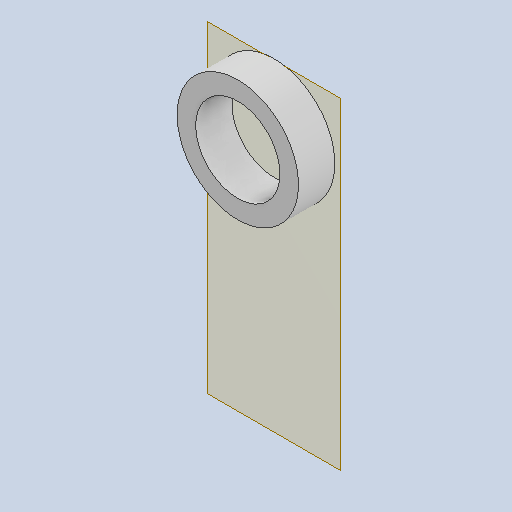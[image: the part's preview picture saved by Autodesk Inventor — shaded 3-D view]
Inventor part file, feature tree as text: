
AUTODESK INVENTOR PART (.ipt)
format: ipt  version: 2023 (Build 270158000, 158)  size: 333,824 bytes
history: native  units: mm
features: other x5, reference x2, plane x1, extrude x1, sketch x1
ambient origin geometry x8: Origin, YZ Plane, XZ Plane, XY Plane, X Axis, Y Axis, Z Axis, Center Point
bodies: Solid1 (feature_tree)
feature tree (10):
  plane  "Work Plane1"
  extrude  "Extrusion1"  Depth=5.5mm TaperAngle=0.0deg
  sketch  "Sketch1"  dims[d0=0.5mm d1=5.5mm d2=0.0mm]
  reference  "Reference1"
  reference  "Reference2"
  parser-record x1  (decoder bookkeeping rows leaked as tree rows — omitted from the tree; the rows remain in map.json)
  other  "doorLockAssembly_V3.iam"
  other  "gear_V3:1"
  other  "pin_V3:1"
  other  "tempMotorHolder_V3:1"
note: 1 file-system path scrubbed to <path> (originals preserved in map.json)
